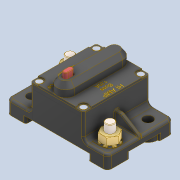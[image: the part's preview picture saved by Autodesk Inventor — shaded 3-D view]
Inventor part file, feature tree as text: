
AUTODESK INVENTOR PART (.ipt)
format: ipt  version: 2021 (Build 250183000, 183)  size: 2,020,864 bytes
history: native  units: in
note: dims shown in document units (in); Inventor stores cm internally (conversion verified against a paired STEP export)
features: sketch x3, extrude x2, other x2, projected_geometry x1
ambient origin geometry x8: Origin, YZ Plane, XZ Plane, XY Plane, X Axis, Y Axis, Z Axis, Center Point
bodies: Solid1 (feature_tree)
feature tree (8):
  extrude  "Extrusion1"  Depth=0.0004in
  sketch  "Sketch2"  dims[d3=0.0004in d4=0.0in]
  extrude  "Extrusion2"  [1 undecoded]
  sketch  "Sketch1"  dims[d0=0.7874in d1=0.0in d2=0.0004in]
  sketch  "Sketch3"
  projected_geometry  "Projected Loop1"
  other  "Composite1"
  other  "Srf1"
note: 1 required parameter value undecoded (feature->parameter linkage not recoverable at this tier; creation-order binding heuristic only, values carry confidence <= 0.55)
